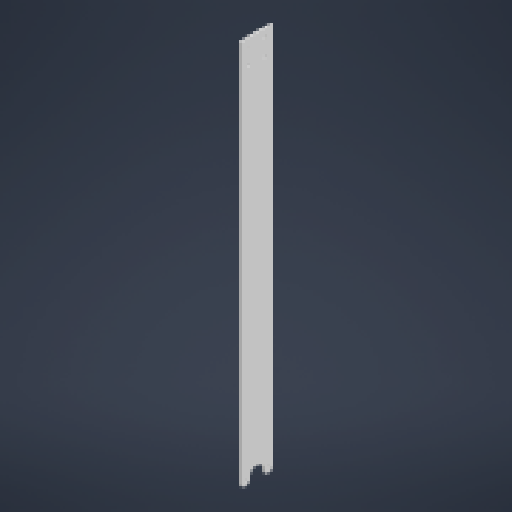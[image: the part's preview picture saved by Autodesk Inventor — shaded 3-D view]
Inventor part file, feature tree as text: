
AUTODESK INVENTOR PART (.ipt)
format: ipt  version: 2024.1 (Build 281209000, 209)  size: 155,648 bytes
history: native  units: in
note: dims shown in document units (in); Inventor stores cm internally (conversion verified against a paired STEP export)
features: extrude x1, fillet x1, sketch x1
ambient origin geometry x8: Origin, YZ Plane, XZ Plane, XY Plane, X Axis, Y Axis, Z Axis, Center Point
bodies: Solid1 (feature_tree)
feature tree (3):
  extrude  "Extrusion1"  Depth=2.0in
  fillet  "Fillet1"  Radius=0.87in
  sketch  "Sketch1"  dims[d0=24.0in d1=2.0in d2=0.87in d3=0.35in d4=0.1575in d5=0.1575in d6=0.3in d7=0.35in d8=0.3in d9=0.35in d10=0.1575in d11=0.1575in d12=0.1575in d13=0.1575in d14=1.0in d15=1.0in d16=1.0in d17=1.0in d18=0.5in d19=0.5in d20=0.1181in d21=0.0in d22=0.25in]
